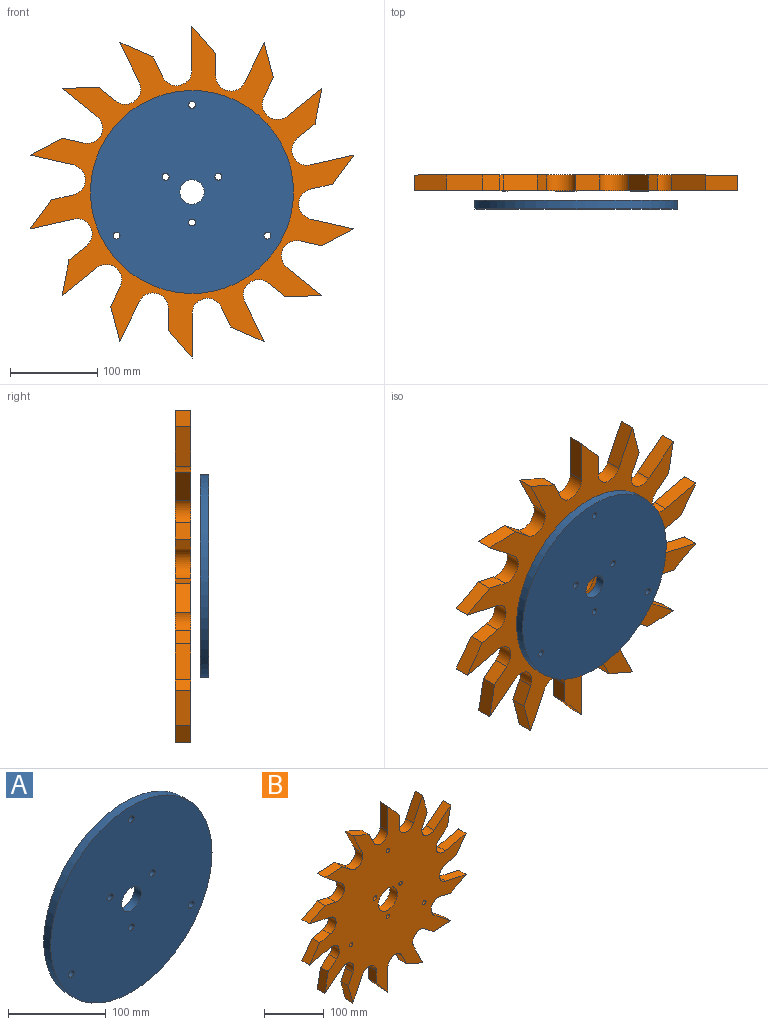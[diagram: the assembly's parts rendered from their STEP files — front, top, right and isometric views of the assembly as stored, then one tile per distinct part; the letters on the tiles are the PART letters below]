
ASSEMBLY  parts=2 mates=1
PART A: 10 faces, bbox 233x10x233 mm
  f0: cylinder r=14mm len=28mm, axis (0,1,0), area 879.6mm2, adj f8,f9
  f1: cylinder r=4mm len=10mm, axis (0,1,0), area 251.3mm2, adj f8,f9
  f2: cylinder r=4mm len=10mm, axis (0,1,0), area 251.3mm2, adj f8,f9
  f3: cylinder r=4mm len=10mm, axis (0,1,0), area 251.3mm2, adj f8,f9
  f4: cylinder r=4mm len=10mm, axis (0,1,0), area 251.3mm2, adj f8,f9
  f5: cylinder r=4mm len=10mm, axis (0,1,0), area 251.3mm2, adj f8,f9
  f6: cylinder r=4mm len=10mm, axis (0,1,0), area 251.3mm2, adj f8,f9
  f7: cylinder r=116.5mm len=233mm, axis (0,1,0), area 7319.9mm2, adj f8,f9
  f8: plane 233x233mm, normal (0,-1,0), area 41721.1mm2, adj f0,f1,f2,f3,f4,f5,f6,f7
  f9: plane 233x233mm, normal (0,1,0), area 41721.1mm2, adj f0,f1,f2,f3,f4,f5,f6,f7
PART B: 65 faces, bbox 371.4x18x381 mm
  f0: plane 24.76x18mm, normal (-0.22,0,-0.97), area 457.2mm2, adj f1,f62,f63,f64
  f1: plane 36.84x19.43mm, normal (0.47,0,-0.88), area 749.8mm2, adj f0,f2,f63,f64
  f2: plane 49.53x18mm, normal (0.22,0,0.97), area 914.4mm2, adj f1,f3,f63,f64
  f3: cylinder r=17.61mm len=34.33mm, axis (0,1,0), area 853.4mm2, adj f2,f4,f63,f64
  f4: plane 24.76x18mm, normal (0.22,0,-0.97), area 457.2mm2, adj f3,f5,f63,f64
  f5: plane 33.49x24.76mm, normal (0.8,0,-0.59), area 749.8mm2, adj f4,f6,f63,f64
  f6: plane 49.53x18mm, normal (-0.22,0,0.97), area 914.4mm2, adj f5,f7,f63,f64
  f7: cylinder r=17.61mm len=31.37mm, axis (0,1,0), area 853.4mm2, adj f6,f8,f63,f64
  f8: plane 19.86x18mm, normal (0.62,0,-0.78), area 457.2mm2, adj f7,f9,f63,f64
  f9: plane 40.92x18mm, normal (0.98,0,-0.19), area 749.8mm2, adj f8,f10,f63,f64
  f10: plane 39.72x31.67mm, normal (-0.62,0,0.78), area 914.4mm2, adj f9,f11,f63,f64
  f11: cylinder r=17.61mm len=28.59mm, axis (0,1,0), area 853.4mm2, adj f10,f12,f63,f64
  f12: plane 22.88x18mm, normal (0.9,0,-0.43), area 457.2mm2, adj f11,f13,f63,f64
  f13: plane 40.24x18mm, normal (0.97,0,0.26), area 749.8mm2, adj f12,f14,f63,f64
  f14: plane 45.77x22.04mm, normal (-0.9,0,0.43), area 914.4mm2, adj f13,f15,f63,f64
  f15: cylinder r=17.61mm len=33.47mm, axis (0,1,0), area 853.4mm2, adj f14,f16,f63,f64
  f16: plane 25.4x18mm, normal (1,0,0), area 457.2mm2, adj f15,f17,f63,f64
  f17: plane 31.6x27.14mm, normal (0.76,0,0.65), area 749.8mm2, adj f16,f18,f63,f64
  f18: plane 50.8x18mm, normal (-1,0,0), area 914.4mm2, adj f17,f19,f63,f64
  f19: cylinder r=17.61mm len=33.47mm, axis (0,1,0), area 853.4mm2, adj f18,f20,f63,f64
  f20: plane 22.88x18mm, normal (0.9,0,0.43), area 457.2mm2, adj f19,f21,f63,f64
  f21: plane 38.16x18mm, normal (0.4,0,0.92), area 749.8mm2, adj f20,f22,f63,f64
  f22: plane 45.77x22.04mm, normal (-0.9,0,-0.43), area 914.4mm2, adj f21,f23,f63,f64
  f23: cylinder r=17.61mm len=28.59mm, axis (0,1,0), area 853.4mm2, adj f22,f24,f63,f64
  f24: plane 19.86x18mm, normal (0.62,0,0.78), area 457.2mm2, adj f23,f25,f63,f64
  f25: plane 41.63x18mm, normal (-0.04,0,1), area 749.8mm2, adj f24,f26,f63,f64
  f26: plane 39.72x31.67mm, normal (-0.62,0,-0.78), area 914.4mm2, adj f25,f27,f63,f64
  f27: cylinder r=17.61mm len=31.37mm, axis (0,1,0), area 853.4mm2, adj f26,f28,f63,f64
  f28: plane 24.76x18mm, normal (0.22,0,0.97), area 457.2mm2, adj f27,f29,f63,f64
  f29: plane 36.84x19.43mm, normal (-0.47,0,0.88), area 749.8mm2, adj f28,f30,f63,f64
  f30: plane 49.53x18mm, normal (-0.22,0,-0.97), area 914.4mm2, adj f29,f31,f63,f64
  f31: cylinder r=17.61mm len=34.33mm, axis (0,1,0), area 853.4mm2, adj f30,f32,f63,f64
  f32: plane 24.76x18mm, normal (-0.22,0,0.97), area 457.2mm2, adj f31,f33,f63,f64
  f33: plane 33.49x24.76mm, normal (-0.8,0,0.59), area 749.8mm2, adj f32,f34,f63,f64
  f34: plane 49.53x18mm, normal (0.22,0,-0.97), area 914.4mm2, adj f33,f35,f63,f64
  f35: cylinder r=17.61mm len=31.37mm, axis (0,1,0), area 853.4mm2, adj f34,f36,f63,f64
  f36: plane 19.86x18mm, normal (-0.62,0,0.78), area 457.2mm2, adj f35,f37,f63,f64
  f37: plane 40.92x18mm, normal (-0.98,0,0.19), area 749.8mm2, adj f36,f38,f63,f64
  f38: plane 39.72x31.67mm, normal (0.62,0,-0.78), area 914.4mm2, adj f37,f39,f63,f64
  f39: cylinder r=17.61mm len=28.59mm, axis (0,1,0), area 853.4mm2, adj f38,f40,f63,f64
  f40: plane 22.88x18mm, normal (-0.9,0,0.43), area 457.2mm2, adj f39,f41,f63,f64
  f41: plane 40.24x18mm, normal (-0.97,0,-0.26), area 749.8mm2, adj f40,f42,f63,f64
  f42: plane 45.77x22.04mm, normal (0.9,0,-0.43), area 914.4mm2, adj f41,f43,f63,f64
  f43: cylinder r=17.61mm len=33.47mm, axis (0,1,0), area 853.4mm2, adj f42,f44,f63,f64
  f44: plane 25.4x18mm, normal (-1,0,0), area 457.2mm2, adj f43,f45,f63,f64
  f45: plane 31.6x27.14mm, normal (-0.76,0,-0.65), area 749.8mm2, adj f44,f46,f63,f64
  f46: plane 50.8x18mm, normal (1,0,0), area 914.4mm2, adj f45,f47,f63,f64
  f47: cylinder r=17.61mm len=33.47mm, axis (0,1,0), area 853.4mm2, adj f46,f48,f63,f64
  f48: plane 22.88x18mm, normal (-0.9,0,-0.43), area 457.2mm2, adj f47,f49,f63,f64
  f49: plane 38.16x18mm, normal (-0.4,0,-0.92), area 749.8mm2, adj f48,f50,f63,f64
  f50: plane 45.77x22.04mm, normal (0.9,0,0.43), area 914.4mm2, adj f49,f51,f63,f64
  f51: cylinder r=17.61mm len=28.59mm, axis (0,1,0), area 853.4mm2, adj f50,f52,f63,f64
  f52: plane 19.86x18mm, normal (-0.62,0,-0.78), area 457.2mm2, adj f51,f53,f63,f64
  f53: plane 41.63x18mm, normal (0.04,0,-1), area 749.8mm2, adj f52,f54,f63,f64
  f54: plane 39.72x31.67mm, normal (0.62,0,0.78), area 914.4mm2, adj f53,f62,f63,f64
  f55: cylinder r=4mm len=18mm, axis (0,1,0), area 452.4mm2, adj f63,f64
  f56: cylinder r=4mm len=18mm, axis (0,1,0), area 452.4mm2, adj f63,f64
  f57: cylinder r=4mm len=18mm, axis (0,1,0), area 452.4mm2, adj f63,f64
  f58: cylinder r=22.61mm len=45.21mm, axis (0,1,0), area 2556.7mm2, adj f63,f64
  f59: cylinder r=4mm len=18mm, axis (0,1,0), area 452.4mm2, adj f63,f64
  f60: cylinder r=4mm len=18mm, axis (0,1,0), area 452.4mm2, adj f63,f64
  f61: cylinder r=4mm len=18mm, axis (0,1,0), area 452.4mm2, adj f63,f64
  f62: cylinder r=17.61mm len=31.37mm, axis (0,1,0), area 853.4mm2, adj f0,f54,f63,f64
  f63: plane 381x371.45mm, normal (0,-1,0), area 66942.6mm2, adj f0,f1,f2,f3,f4,f5,f6,f7
  f64: plane 381x371.45mm, normal (0,1,0), area 66942.6mm2, adj f0,f1,f2,f3,f4,f5,f6,f7
PLACE A t=(-46.68,-23.8,8.73)mm
PLACE B t=(-46.68,5.2,8.73)mm
MATE slider B.f58 <-> A.f0  axis (0,-1,0) through (-46.68,-12.8,8.73)mm
